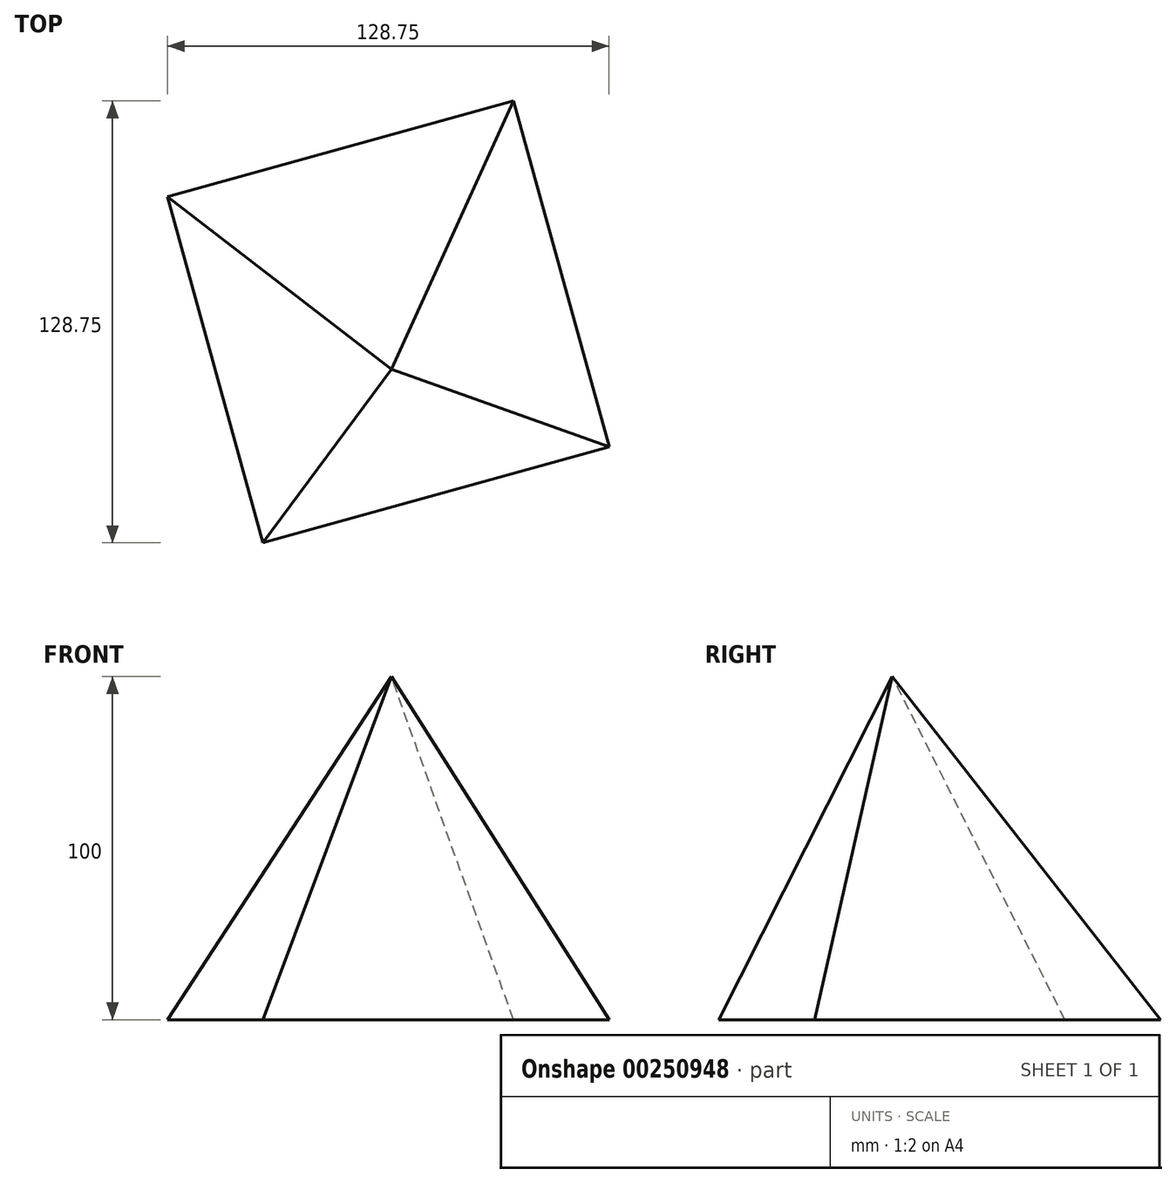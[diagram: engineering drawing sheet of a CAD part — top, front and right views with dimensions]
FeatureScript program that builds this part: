
annotation { "Feature Type Name" : "Feature", "Feature Type Description" : "" }
export const myFeature = defineFeature(function(context is Context, id is Id, definition is map)
    precondition{}
    {
        {
            var Q0;
            Q0=qCreatedBy(makeId("Top.planeOp"),FACE);
            var sketch = newSketch(context, id + "F0", { "sketchPlane" : qUnion([Q0])});
            skCircle(sketch, "E0.cCircle", {"center": v(-4.3, 12.2) * mm, "radius": 73.99 * mm, "construction": true});
            skLineSegment(sketch, "E0.0", {"start": v(-40.77, -52.18) * mm, "end": v(-68.68, 48.66) * mm});
            skLineSegment(sketch, "E0.1", {"start": v(-68.68, 48.66) * mm, "end": v(32.16, 76.57) * mm});
            skLineSegment(sketch, "E0.2", {"start": v(32.16, 76.57) * mm, "end": v(60.07, -24.28) * mm});
            skLineSegment(sketch, "E0.3", {"start": v(60.07, -24.28) * mm, "end": v(-40.77, -52.18) * mm});
            skSolve(sketch);
        }
        {
            var Q0;
            Q0=qCreatedBy(makeId("Top.planeOp"),FACE);
            cPlane(context, id + "F1", {"entities" : qUnion([Q0]), "cplaneType" : CPlaneType.OFFSET, "offset" : 100 * mm, "width" : 150 * mm, "height" : 150 * mm});
        }
        {
            var Q0;
            Q0=qCreatedBy(id+"F1.planeOp",FACE);
            var sketch = newSketch(context, id + "F2", { "sketchPlane" : qUnion([Q0])});
            skPoint(sketch, "E1", {"position": v(-3.36, -1.65) * mm});
            skSolve(sketch);
        }
        {
            var Q0;
            Q0=makeQuery(id+"F0.imprint","IMPRINT",FACE,{"disambiguationData":[TD([[makeQuery(id+"F0.imprint","IMPRINT",EDGE,{"derivedFrom":sQuery(id+"F0.wireOp",EDGE,"E0.0")}),-1.0]])]});
            var Q1;
            Q1=sQuery(id+"F2.wireOp",VERTEX,"E1");
            loft(context, id + "F3", {"sheetProfilesArray" : [{ "sheetProfileEntities" : qUnion([Q0]) }, { "sheetProfileEntities" : qUnion([Q1]) }]});
        }
    });
